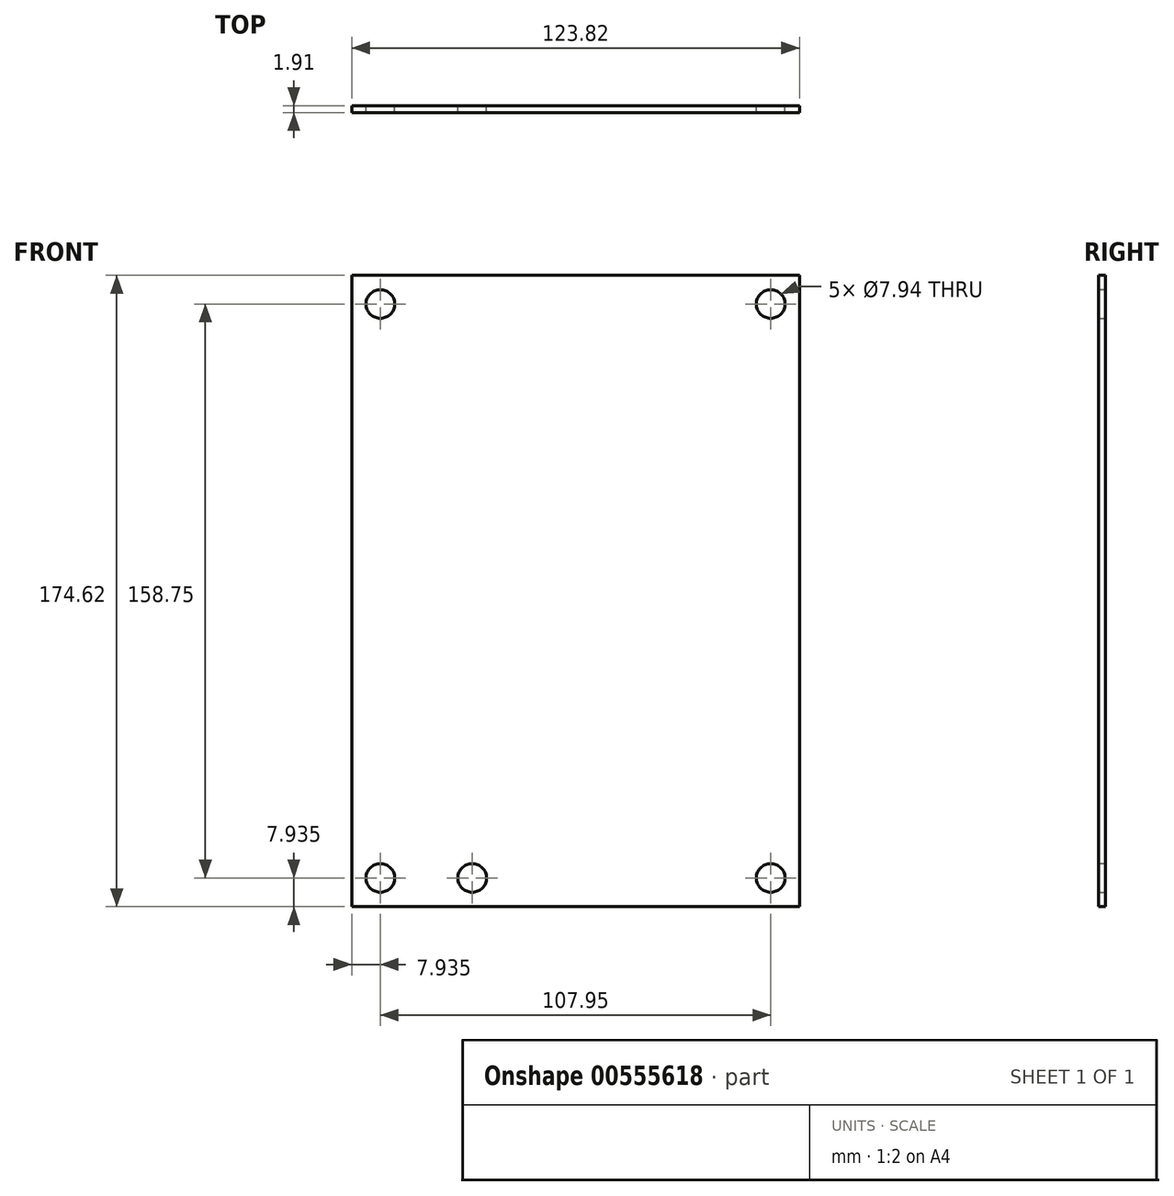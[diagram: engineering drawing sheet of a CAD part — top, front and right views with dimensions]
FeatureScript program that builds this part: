
annotation { "Feature Type Name" : "Feature", "Feature Type Description" : "" }
export const myFeature = defineFeature(function(context is Context, id is Id, definition is map)
    precondition{}
    {
        {
            var Q0;
            Q0=qCreatedBy(makeId("Front.planeOp"),FACE);
            var sketch = newSketch(context, id + "F0", { "sketchPlane" : qUnion([Q0])});
            skLineSegment(sketch, "E0.bottom", {"start": v(61.91, 87.31) * mm, "end": v(-61.91, 87.31) * mm});
            skLineSegment(sketch, "E0.top", {"start": v(61.91, -87.31) * mm, "end": v(-61.91, -87.31) * mm});
            skLineSegment(sketch, "E0.left", {"start": v(61.91, 87.31) * mm, "end": v(61.91, -87.31) * mm});
            skLineSegment(sketch, "E0.right", {"start": v(-61.91, 87.31) * mm, "end": v(-61.91, -87.31) * mm});
            skPoint(sketch, "E0.middle", {"position": v(0, 0) * mm});
            skCircle(sketch, "E1", {"center": v(-53.97, 79.38) * mm, "radius": 3.97 * mm});
            skCircle(sketch, "E2", {"center": v(53.98, 79.38) * mm, "radius": 3.97 * mm});
            skCircle(sketch, "E3", {"center": v(-53.98, -79.38) * mm, "radius": 3.97 * mm});
            skCircle(sketch, "E4", {"center": v(53.97, -79.38) * mm, "radius": 3.97 * mm});
            skCircle(sketch, "E5", {"center": v(-28.58, -79.38) * mm, "radius": 3.97 * mm});
            skSolve(sketch);
        }
        {
            var Q0;
            Q0 = qSketchRegion(id + "F0", true);
            extrude(context, id + "F1", {"entities" : qUnion([Q0]), "depth" : 1.9 * mm, "offsetDistance" : 25.4 * mm});
        }
    });
